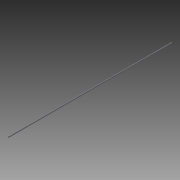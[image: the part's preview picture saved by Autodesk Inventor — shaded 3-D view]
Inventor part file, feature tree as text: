
AUTODESK INVENTOR PART (.ipt)
format: ipt  version: 2013 (Build 170138000, 138)  size: 76,800 bytes
history: native  units: in
note: dims shown in document units (in); Inventor stores cm internally (conversion verified against a paired STEP export)
features: plane x1, extrude x1, sketch x1
ambient origin geometry x8: Origin, YZ Plane, XZ Plane, XY Plane, X Axis, Y Axis, Z Axis, Center Point
feature tree (3):
  plane  "Work Plane1"
  extrude  "Extrusion1"  [1 undecoded]
  sketch  "Sketch1"  dims[d0=50.0in d1=0.0in]
note: 1 required parameter value undecoded (feature->parameter linkage not recoverable at this tier; creation-order binding heuristic only, values carry confidence <= 0.55)
